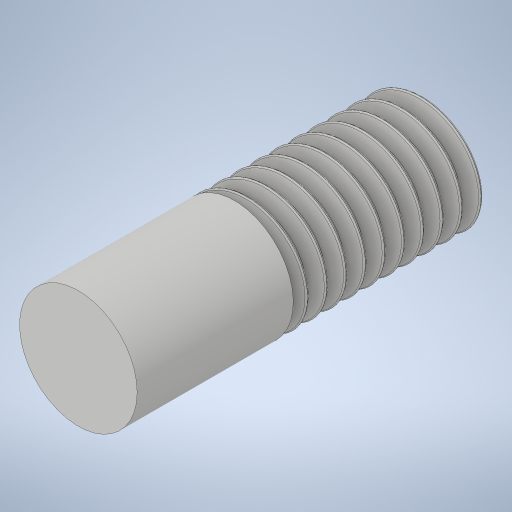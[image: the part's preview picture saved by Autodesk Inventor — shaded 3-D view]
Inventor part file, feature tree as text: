
AUTODESK INVENTOR PART (.ipt)
format: ipt  version: 2023 (Build 270158000, 158)  size: 745,984 bytes
history: native  units: mm
features: sketch x4, revolve x2, extrude x1, thread x1, helix x1, boolean_combine x1
ambient origin geometry x8: Origin, YZ Plane, XZ Plane, XY Plane, X Axis, Y Axis, Z Axis, Center Point
bodies: Solid1 (feature_tree), Solid2 (feature_tree)
feature tree (10):
  extrude  "Extrusion1"  Depth=18.1mm TaperAngle=0.0deg
  thread  "Thread1"  [1 undecoded]
  revolve  "Revolution1"  [1 undecoded]
  revolve  "Revolution2"  [1 undecoded]
  helix  "Coil1"  [1 undecoded]
  boolean_combine  "Combine1"
  sketch  "Sketch1"  dims[d0=6.1mm d1=18.1mm d2=0.0mm d3=10.0mm d4=0.0mm]
  sketch  "Sketch2"  dims[d5=9.599311mm d6=0.160083mm d7=0.160083mm d10=1.0mm]
  sketch  "Sketch3"  dims[d12=9.599311mm d14=0.0mm d15=0.0mm]
  sketch  "Sketch4"  dims[d16=1.001mm d17=12.0mm d18=10.0mm d19=0.0mm d20=0.0mm d21=0.0mm d22=0.0mm d23=0.0mm]
note: 4 required parameter values undecoded (feature->parameter linkage not recoverable at this tier; creation-order binding heuristic only, values carry confidence <= 0.55)